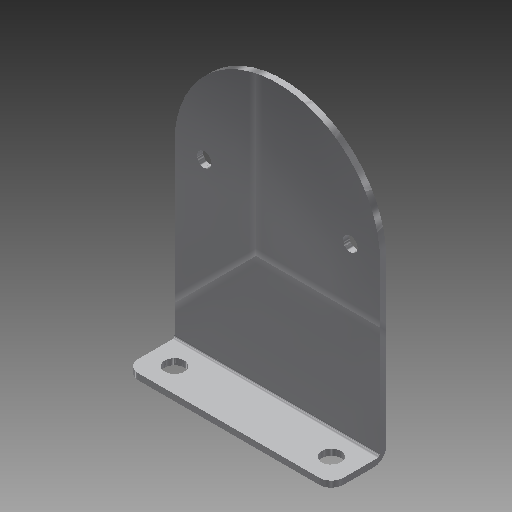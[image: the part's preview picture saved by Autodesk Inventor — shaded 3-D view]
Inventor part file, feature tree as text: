
AUTODESK INVENTOR PART (.ipt)
format: ipt  version: 2017 (Build 210142000, 142)  size: 140,288 bytes
history: native  units: in
note: dims shown in document units (in); Inventor stores cm internally (conversion verified against a paired STEP export)
features: fillet x3, hole x3, sketch x3, extrude x2, reference x2
ambient origin geometry x8: Origin, YZ Plane, XZ Plane, XY Plane, X Axis, Y Axis, Z Axis, Center Point
bodies: Solid1 (feature_tree)
feature tree (13):
  extrude  "Extrusion1"  Depth=0.0625in
  extrude  "Extrusion2"  Depth=0.125in
  fillet  "Fillet1"  Radius=0.0312in
  hole  "Hole1"  [1 undecoded]
  fillet  "Fillet2"  Radius=0.75in
  hole  "Hole2"  [1 undecoded]
  hole  "Hole3"  [1 undecoded]
  fillet  "Fillet3"  [1 undecoded]
  sketch  "Sketch1"  dims[d0=0.0625in d1=0.0in d2=0.0625in]
  reference  "Reference1"
  sketch  "Sketch2"  dims[d3=0.5in d4=0.0in d5=0.125in]
  sketch  "Sketch3"  dims[d6=0.25in d16=0.25in d8=0.201in d9=0.75in d10=0.385in d11=0.25in d12=0.5635in d13=1.0in d14=0.8108in d15=0.0312in d17=0.25in d18=0.25in d19=0.201in d20=0.75in d21=0.385in d22=0.25in d23=0.5635in d24=1.0in d25=0.8108in d26=0.75in d27=0.75in d28=0.15in d29=0.75in d30=0.385in d31=0.25in d32=0.5635in d33=1.0in d34=0.8108in d35=0.125in]
  reference  "Reference3"
note: 4 required parameter values undecoded (feature->parameter linkage not recoverable at this tier; creation-order binding heuristic only, values carry confidence <= 0.55)
